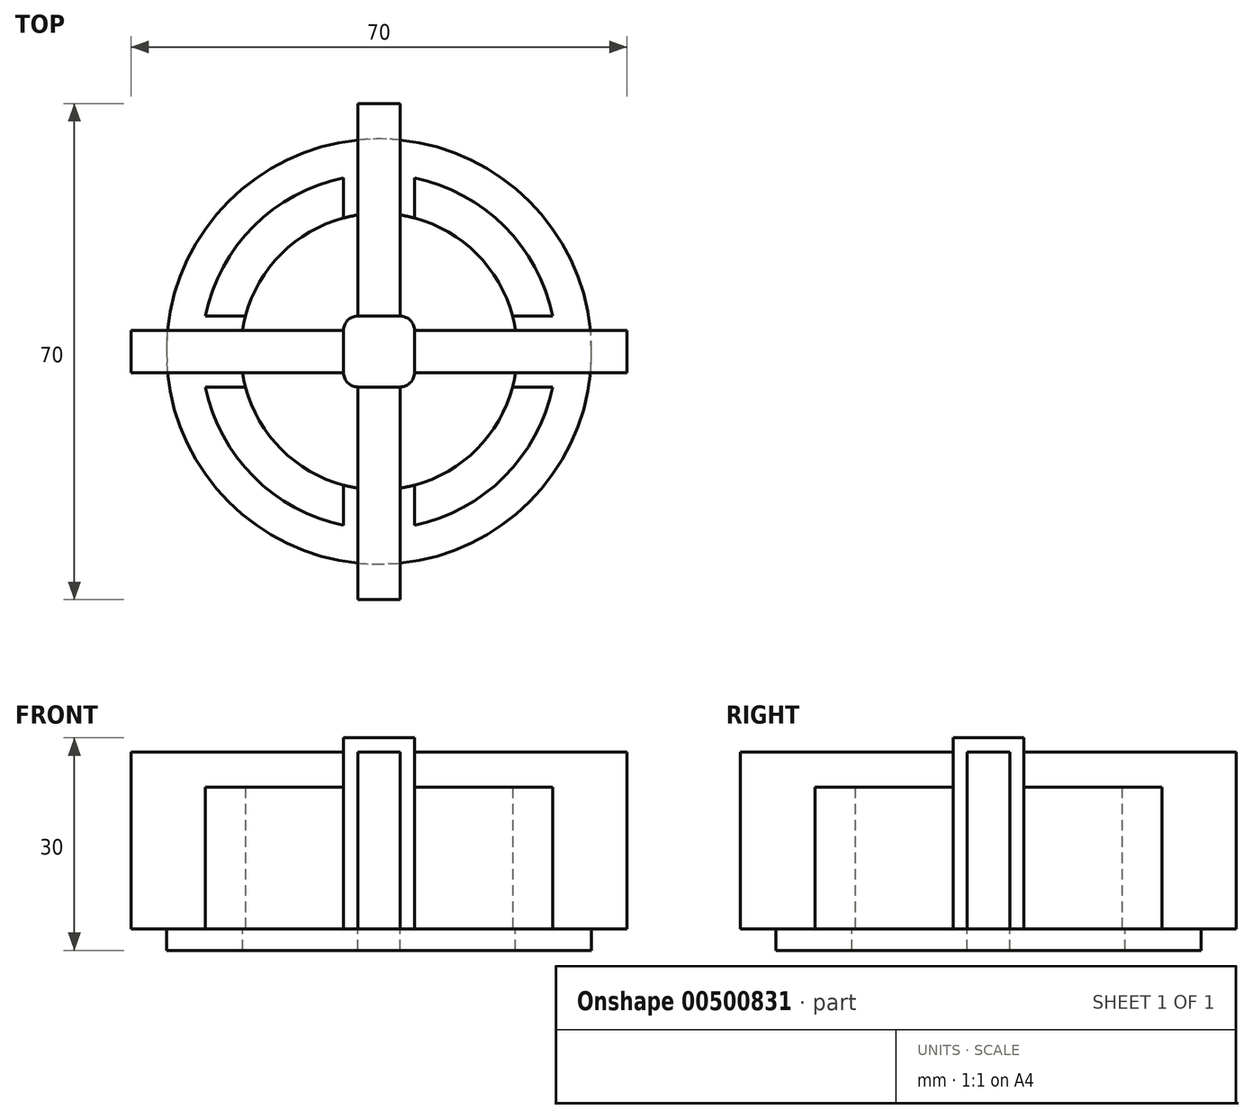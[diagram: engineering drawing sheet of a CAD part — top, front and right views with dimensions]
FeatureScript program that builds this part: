
annotation { "Feature Type Name" : "Feature", "Feature Type Description" : "" }
export const myFeature = defineFeature(function(context is Context, id is Id, definition is map)
    precondition{}
    {
        {
            var Q0;
            Q0=qCreatedBy(makeId("Top.planeOp"),FACE);
            var sketch = newSketch(context, id + "F0", { "sketchPlane" : qUnion([Q0])});
            skCircle(sketch, "E0", {"center": v(0, 0) * mm, "radius": 25 * mm});
            skCircle(sketch, "E1.0", {"center": v(0, 0) * mm, "radius": 19.5 * mm});
            skLineSegment(sketch, "E2", {"start": v(0, 0) * mm, "end": v(0, -5) * mm, "construction": true});
            skLineSegment(sketch, "E3", {"start": v(-3, -5) * mm, "end": v(3, -5) * mm});
            skPoint(sketch, "E4", {"position": v(0, -5) * mm});
            skLineSegment(sketch, "E5", {"start": v(5, -3) * mm, "end": v(5, 3) * mm});
            skLineSegment(sketch, "E6", {"start": v(3, 5) * mm, "end": v(-3, 5) * mm});
            skLineSegment(sketch, "E7", {"start": v(-5, 3) * mm, "end": v(-5, -3) * mm});
            skLineSegment(sketch, "E8", {"start": v(-3, -5) * mm, "end": v(3, -5) * mm, "construction": true});
            skLineSegment(sketch, "E9", {"start": v(-3, -5) * mm, "end": v(-3, -35) * mm});
            skLineSegment(sketch, "E10", {"start": v(-3, -35) * mm, "end": v(3, -35) * mm});
            skLineSegment(sketch, "E11", {"start": v(3, -35) * mm, "end": v(3, -5) * mm});
            skLineSegment(sketch, "E12", {"start": v(5, 3) * mm, "end": v(5, -3) * mm, "construction": true});
            skPoint(sketch, "E13", {"position": v(5, 0) * mm});
            skLineSegment(sketch, "E14", {"start": v(0, 0) * mm, "end": v(5, 0) * mm, "construction": true});
            skLineSegment(sketch, "E15", {"start": v(5, 3) * mm, "end": v(35, 3) * mm});
            skLineSegment(sketch, "E16", {"start": v(35, 3) * mm, "end": v(35, -3) * mm});
            skLineSegment(sketch, "E17", {"start": v(35, -3) * mm, "end": v(5, -3) * mm});
            skLineSegment(sketch, "E18", {"start": v(0, -35) * mm, "end": v(0, -30) * mm, "construction": true});
            skLineSegment(sketch, "E19", {"start": v(3, -30) * mm, "end": v(-3, -30) * mm, "construction": true});
            skLineSegment(sketch, "E20", {"start": v(35, 0) * mm, "end": v(30, 0) * mm, "construction": true});
            skLineSegment(sketch, "E21", {"start": v(30, -3) * mm, "end": v(30, 3) * mm, "construction": true});
            skLineSegment(sketch, "E22", {"start": v(24.5, 0) * mm, "end": v(24.5, 5) * mm, "construction": true});
            skLineSegment(sketch, "E23", {"start": v(24.5, 5) * mm, "end": v(18.85, 5) * mm});
            skLineSegment(sketch, "E24.MirrorCS", {"start": v(24.5, 0) * mm, "end": v(24.5, -5) * mm, "construction": true});
            skLineSegment(sketch, "E25.MirrorCS", {"start": v(24.5, -5) * mm, "end": v(18.85, -5) * mm});
            skLineSegment(sketch, "E26", {"start": v(0, -24.5) * mm, "end": v(5, -24.5) * mm, "construction": true});
            skPoint(sketch, "E27.visualSharp", {"position": v(5, -5) * mm});
            skArc(sketch, "E27.filletArc", {"start": v(3, -5) * mm, "mid": v(4.41, -4.41) * mm, "end": v(5, -3) * mm});
            skPoint(sketch, "E28.visualSharp", {"position": v(5, 5) * mm});
            skArc(sketch, "E28.filletArc", {"start": v(5, 3) * mm, "mid": v(4.41, 4.41) * mm, "end": v(3, 5) * mm});
            skPoint(sketch, "E29.visualSharp", {"position": v(-5, 5) * mm});
            skArc(sketch, "E29.filletArc", {"start": v(-3, 5) * mm, "mid": v(-4.41, 4.41) * mm, "end": v(-5, 3) * mm});
            skPoint(sketch, "E30.visualSharp", {"position": v(-5, -5) * mm});
            skArc(sketch, "E30.filletArc", {"start": v(-5, -3) * mm, "mid": v(-4.41, -4.41) * mm, "end": v(-3, -5) * mm});
            skLineSegment(sketch, "E31.MirrorCS", {"start": v(3, 35) * mm, "end": v(3, 5) * mm});
            skLineSegment(sketch, "E32.MirrorCS", {"start": v(-3, 5) * mm, "end": v(-3, 35) * mm});
            skLineSegment(sketch, "E33.MirrorCS", {"start": v(3, 30) * mm, "end": v(-3, 30) * mm, "construction": true});
            skLineSegment(sketch, "E34.MirrorCS", {"start": v(0, 35) * mm, "end": v(0, 30) * mm, "construction": true});
            skLineSegment(sketch, "E35.MirrorCS", {"start": v(-3, 35) * mm, "end": v(3, 35) * mm});
            skLineSegment(sketch, "E36.MirrorCS", {"start": v(0, -24.5) * mm, "end": v(-5, -24.5) * mm, "construction": true});
            skLineSegment(sketch, "E37", {"start": v(5, -24.5) * mm, "end": v(5, -18.85) * mm});
            skLineSegment(sketch, "E38.MirrorCS", {"start": v(-5, -24.5) * mm, "end": v(-5, -18.85) * mm});
            skLineSegment(sketch, "E39.MirrorCS", {"start": v(5, 24.5) * mm, "end": v(5, 18.85) * mm});
            skLineSegment(sketch, "E40.MirrorCS", {"start": v(-5, 24.5) * mm, "end": v(-5, 18.85) * mm});
            skLineSegment(sketch, "E41.MirrorCS", {"start": v(-35, -3) * mm, "end": v(-5, -3) * mm});
            skLineSegment(sketch, "E42.MirrorCS", {"start": v(-5, 3) * mm, "end": v(-35, 3) * mm});
            skLineSegment(sketch, "E43.MirrorCS", {"start": v(-24.5, -5) * mm, "end": v(-18.85, -5) * mm});
            skLineSegment(sketch, "E44.MirrorCS", {"start": v(-24.5, 5) * mm, "end": v(-18.85, 5) * mm});
            skLineSegment(sketch, "E45.MirrorCS", {"start": v(-30, -3) * mm, "end": v(-30, 3) * mm, "construction": true});
            skLineSegment(sketch, "E46.MirrorCS", {"start": v(-35, 3) * mm, "end": v(-35, -3) * mm});
            skCircle(sketch, "E47", {"center": v(0, 0) * mm, "radius": 30 * mm});
            skSolve(sketch);
        }
        {
            var Q0;
            {var subQ0=sQuery(id+"F0.wireOp",EDGE,"E0");var subQ4=makeQuery(id+"F0.imprint","INTERSECT",VERTEX,{"derivedFrom":[subQ0,sQuery(id+"F0.wireOp",EDGE,"E37")]});Q0=makeQuery(id+"F0.imprint","IMPRINT",FACE,{"disambiguationData":[TD([[makeQuery(id+"F0.imprint","IMPRINT",EDGE,{"disambiguationData":[TD([[subQ4,1.0]])],"derivedFrom":subQ0}),-1.0]])]});}
            var Q1;
            {var subQ0=sQuery(id+"F0.wireOp",EDGE,"E25.MirrorCS");Q1=makeQuery(id+"F0.imprint","IMPRINT",FACE,{"disambiguationData":[TD([[makeQuery(id+"F0.imprint","IMPRINT",EDGE,{"derivedFrom":subQ0}),1.0]])]});}
            var Q2;
            {var subQ0=sQuery(id+"F0.wireOp",EDGE,"E25.MirrorCS");Q2=makeQuery(id+"F0.imprint","IMPRINT",FACE,{"disambiguationData":[TD([[makeQuery(id+"F0.imprint","IMPRINT",EDGE,{"derivedFrom":subQ0}),-1.0]])]});}
            var Q3;
            {var subQ0=sQuery(id+"F0.wireOp",EDGE,"E15");var subQ1=sQuery(id+"F0.wireOp",EDGE,"E0");var subQ2=makeQuery(id+"F0.imprint","INTERSECT",VERTEX,{"derivedFrom":[subQ1,subQ0]});Q3=makeQuery(id+"F0.imprint","IMPRINT",FACE,{"disambiguationData":[TD([[makeQuery(id+"F0.imprint","IMPRINT",EDGE,{"disambiguationData":[TD([[subQ2,1.0]])],"derivedFrom":subQ1}),1.0]])]});}
            var Q4;
            {var subQ0=sQuery(id+"F0.wireOp",EDGE,"E23");Q4=makeQuery(id+"F0.imprint","IMPRINT",FACE,{"disambiguationData":[TD([[makeQuery(id+"F0.imprint","IMPRINT",EDGE,{"derivedFrom":subQ0}),1.0]])]});}
            var Q5;
            {var subQ0=sQuery(id+"F0.wireOp",EDGE,"E23");Q5=makeQuery(id+"F0.imprint","IMPRINT",FACE,{"disambiguationData":[TD([[makeQuery(id+"F0.imprint","IMPRINT",EDGE,{"derivedFrom":subQ0}),-1.0]])]});}
            var Q6;
            {var subQ3=sQuery(id+"F0.wireOp",EDGE,"E0");var subQ8=makeQuery(id+"F0.imprint","INTERSECT",VERTEX,{"derivedFrom":[subQ3,sQuery(id+"F0.wireOp",EDGE,"E23")]});Q6=makeQuery(id+"F0.imprint","IMPRINT",FACE,{"disambiguationData":[TD([[makeQuery(id+"F0.imprint","IMPRINT",EDGE,{"disambiguationData":[TD([[subQ8,1.0]])],"derivedFrom":subQ3}),-1.0]])]});}
            var Q7;
            {var subQ0=sQuery(id+"F0.wireOp",EDGE,"E15");var subQ1=sQuery(id+"F0.wireOp",EDGE,"E0");var subQ2=makeQuery(id+"F0.imprint","INTERSECT",VERTEX,{"derivedFrom":[subQ1,subQ0]});Q7=makeQuery(id+"F0.imprint","IMPRINT",FACE,{"disambiguationData":[TD([[makeQuery(id+"F0.imprint","IMPRINT",EDGE,{"disambiguationData":[TD([[subQ2,1.0]])],"derivedFrom":subQ1}),-1.0]])]});}
            var Q8;
            {var subQ0=sQuery(id+"F0.wireOp",EDGE,"E9");var subQ1=sQuery(id+"F0.wireOp",EDGE,"E0");var subQ2=makeQuery(id+"F0.imprint","INTERSECT",VERTEX,{"derivedFrom":[subQ1,subQ0]});Q8=makeQuery(id+"F0.imprint","IMPRINT",FACE,{"disambiguationData":[TD([[makeQuery(id+"F0.imprint","IMPRINT",EDGE,{"disambiguationData":[TD([[subQ2,-1.0]])],"derivedFrom":subQ1}),-1.0]])]});}
            var Q9;
            {var subQ0=sQuery(id+"F0.wireOp",EDGE,"E9");var subQ1=sQuery(id+"F0.wireOp",EDGE,"E0");var subQ2=makeQuery(id+"F0.imprint","INTERSECT",VERTEX,{"derivedFrom":[subQ1,subQ0]});Q9=makeQuery(id+"F0.imprint","IMPRINT",FACE,{"disambiguationData":[TD([[makeQuery(id+"F0.imprint","IMPRINT",EDGE,{"disambiguationData":[TD([[subQ2,-1.0]])],"derivedFrom":subQ1}),1.0]])]});}
            var Q10;
            {var subQ0=sQuery(id+"F0.wireOp",EDGE,"E37");Q10=makeQuery(id+"F0.imprint","IMPRINT",FACE,{"disambiguationData":[TD([[makeQuery(id+"F0.imprint","IMPRINT",EDGE,{"derivedFrom":subQ0}),1.0]])]});}
            var Q11;
            {var subQ0=sQuery(id+"F0.wireOp",EDGE,"E38.MirrorCS");Q11=makeQuery(id+"F0.imprint","IMPRINT",FACE,{"disambiguationData":[TD([[makeQuery(id+"F0.imprint","IMPRINT",EDGE,{"derivedFrom":subQ0}),-1.0]])]});}
            var Q12;
            {var subQ0=sQuery(id+"F0.wireOp",EDGE,"E0");var subQ4=makeQuery(id+"F0.imprint","INTERSECT",VERTEX,{"derivedFrom":[subQ0,sQuery(id+"F0.wireOp",EDGE,"E43.MirrorCS")]});Q12=makeQuery(id+"F0.imprint","IMPRINT",FACE,{"disambiguationData":[TD([[makeQuery(id+"F0.imprint","IMPRINT",EDGE,{"disambiguationData":[TD([[subQ4,1.0]])],"derivedFrom":subQ0}),-1.0]])]});}
            var Q13;
            {var subQ0=sQuery(id+"F0.wireOp",EDGE,"E38.MirrorCS");Q13=makeQuery(id+"F0.imprint","IMPRINT",FACE,{"disambiguationData":[TD([[makeQuery(id+"F0.imprint","IMPRINT",EDGE,{"derivedFrom":subQ0}),1.0]])]});}
            var Q14;
            {var subQ0=sQuery(id+"F0.wireOp",EDGE,"E43.MirrorCS");Q14=makeQuery(id+"F0.imprint","IMPRINT",FACE,{"disambiguationData":[TD([[makeQuery(id+"F0.imprint","IMPRINT",EDGE,{"derivedFrom":subQ0}),1.0]])]});}
            var Q15;
            {var subQ0=sQuery(id+"F0.wireOp",EDGE,"E42.MirrorCS");var subQ1=sQuery(id+"F0.wireOp",EDGE,"E0");var subQ2=makeQuery(id+"F0.imprint","INTERSECT",VERTEX,{"derivedFrom":[subQ1,subQ0]});Q15=makeQuery(id+"F0.imprint","IMPRINT",FACE,{"disambiguationData":[TD([[makeQuery(id+"F0.imprint","IMPRINT",EDGE,{"disambiguationData":[TD([[subQ2,-1.0]])],"derivedFrom":subQ1}),1.0]])]});}
            var Q16;
            {var subQ0=sQuery(id+"F0.wireOp",EDGE,"E44.MirrorCS");Q16=makeQuery(id+"F0.imprint","IMPRINT",FACE,{"disambiguationData":[TD([[makeQuery(id+"F0.imprint","IMPRINT",EDGE,{"derivedFrom":subQ0}),-1.0]])]});}
            var Q17;
            {var subQ3=sQuery(id+"F0.wireOp",EDGE,"E0");var subQ8=makeQuery(id+"F0.imprint","INTERSECT",VERTEX,{"derivedFrom":[subQ3,sQuery(id+"F0.wireOp",EDGE,"E40.MirrorCS")]});Q17=makeQuery(id+"F0.imprint","IMPRINT",FACE,{"disambiguationData":[TD([[makeQuery(id+"F0.imprint","IMPRINT",EDGE,{"disambiguationData":[TD([[subQ8,1.0]])],"derivedFrom":subQ3}),-1.0]])]});}
            var Q18;
            {var subQ0=sQuery(id+"F0.wireOp",EDGE,"E40.MirrorCS");Q18=makeQuery(id+"F0.imprint","IMPRINT",FACE,{"disambiguationData":[TD([[makeQuery(id+"F0.imprint","IMPRINT",EDGE,{"derivedFrom":subQ0}),-1.0]])]});}
            var Q19;
            {var subQ0=sQuery(id+"F0.wireOp",EDGE,"E40.MirrorCS");Q19=makeQuery(id+"F0.imprint","IMPRINT",FACE,{"disambiguationData":[TD([[makeQuery(id+"F0.imprint","IMPRINT",EDGE,{"derivedFrom":subQ0}),1.0]])]});}
            var Q20;
            {var subQ0=sQuery(id+"F0.wireOp",EDGE,"E31.MirrorCS");var subQ1=sQuery(id+"F0.wireOp",EDGE,"E0");var subQ2=makeQuery(id+"F0.imprint","INTERSECT",VERTEX,{"derivedFrom":[subQ1,subQ0]});Q20=makeQuery(id+"F0.imprint","IMPRINT",FACE,{"disambiguationData":[TD([[makeQuery(id+"F0.imprint","IMPRINT",EDGE,{"disambiguationData":[TD([[subQ2,-1.0]])],"derivedFrom":subQ1}),1.0]])]});}
            var Q21;
            {var subQ0=sQuery(id+"F0.wireOp",EDGE,"E39.MirrorCS");Q21=makeQuery(id+"F0.imprint","IMPRINT",FACE,{"disambiguationData":[TD([[makeQuery(id+"F0.imprint","IMPRINT",EDGE,{"derivedFrom":subQ0}),-1.0]])]});}
            var Q22;
            {var subQ0=sQuery(id+"F0.wireOp",EDGE,"E31.MirrorCS");var subQ1=sQuery(id+"F0.wireOp",EDGE,"E0");var subQ2=makeQuery(id+"F0.imprint","INTERSECT",VERTEX,{"derivedFrom":[subQ1,subQ0]});Q22=makeQuery(id+"F0.imprint","IMPRINT",FACE,{"disambiguationData":[TD([[makeQuery(id+"F0.imprint","IMPRINT",EDGE,{"disambiguationData":[TD([[subQ2,-1.0]])],"derivedFrom":subQ1}),-1.0]])]});}
            var Q23;
            {var subQ0=sQuery(id+"F0.wireOp",EDGE,"E42.MirrorCS");var subQ1=sQuery(id+"F0.wireOp",EDGE,"E0");var subQ2=makeQuery(id+"F0.imprint","INTERSECT",VERTEX,{"derivedFrom":[subQ1,subQ0]});Q23=makeQuery(id+"F0.imprint","IMPRINT",FACE,{"disambiguationData":[TD([[makeQuery(id+"F0.imprint","IMPRINT",EDGE,{"disambiguationData":[TD([[subQ2,-1.0]])],"derivedFrom":subQ1}),-1.0]])]});}
            var Q24;
            {var subQ5=sQuery(id+"F0.wireOp",EDGE,"E3");Q24=makeQuery(id+"F0.imprint","IMPRINT",FACE,{"disambiguationData":[TD([[makeQuery(id+"F0.imprint","IMPRINT",EDGE,{"derivedFrom":subQ5}),-1.0]])]});}
            var Q25;
            {var subQ5=sQuery(id+"F0.wireOp",EDGE,"E5");Q25=makeQuery(id+"F0.imprint","IMPRINT",FACE,{"disambiguationData":[TD([[makeQuery(id+"F0.imprint","IMPRINT",EDGE,{"derivedFrom":subQ5}),-1.0]])]});}
            var Q26;
            {var subQ5=sQuery(id+"F0.wireOp",EDGE,"E6");Q26=makeQuery(id+"F0.imprint","IMPRINT",FACE,{"disambiguationData":[TD([[makeQuery(id+"F0.imprint","IMPRINT",EDGE,{"derivedFrom":subQ5}),-1.0]])]});}
            var Q27;
            {var subQ5=sQuery(id+"F0.wireOp",EDGE,"E7");Q27=makeQuery(id+"F0.imprint","IMPRINT",FACE,{"disambiguationData":[TD([[makeQuery(id+"F0.imprint","IMPRINT",EDGE,{"derivedFrom":subQ5}),-1.0]])]});}
            var Q28;
            Q28=makeQuery(id+"F0.imprint","IMPRINT",FACE,{"disambiguationData":[TD([[makeQuery(id+"F0.imprint","IMPRINT",EDGE,{"derivedFrom":sQuery(id+"F0.wireOp",EDGE,"E3")}),1.0]])]});
            extrude(context, id + "F1", {"entities" : qUnion([Q0, Q1, Q2, Q3, Q4, Q5, Q6, Q7, Q8, Q9, Q10, Q11, Q12, Q13, Q14, Q15, Q16, Q17, Q18, Q19, Q20, Q21, Q22, Q23, Q24, Q25, Q26, Q27, Q28]), "oppositeDirection" : true, "depth" : 3 * mm});
        }
        {
            var Q0;
            {var subQ0=sQuery(id+"F0.wireOp",EDGE,"E40.MirrorCS");Q0=makeQuery(id+"F0.imprint","IMPRINT",FACE,{"disambiguationData":[TD([[makeQuery(id+"F0.imprint","IMPRINT",EDGE,{"derivedFrom":subQ0}),-1.0]])]});}
            var Q1;
            {var subQ0=sQuery(id+"F0.wireOp",EDGE,"E23");Q1=makeQuery(id+"F0.imprint","IMPRINT",FACE,{"disambiguationData":[TD([[makeQuery(id+"F0.imprint","IMPRINT",EDGE,{"derivedFrom":subQ0}),-1.0]])]});}
            var Q2;
            {var subQ0=sQuery(id+"F0.wireOp",EDGE,"E25.MirrorCS");Q2=makeQuery(id+"F0.imprint","IMPRINT",FACE,{"disambiguationData":[TD([[makeQuery(id+"F0.imprint","IMPRINT",EDGE,{"derivedFrom":subQ0}),1.0]])]});}
            var Q3;
            {var subQ0=sQuery(id+"F0.wireOp",EDGE,"E38.MirrorCS");Q3=makeQuery(id+"F0.imprint","IMPRINT",FACE,{"disambiguationData":[TD([[makeQuery(id+"F0.imprint","IMPRINT",EDGE,{"derivedFrom":subQ0}),1.0]])]});}
            extrude(context, id + "F2", {"entities" : qUnion([Q0, Q1, Q2, Q3]), "operationType" : NewBodyOperationType.ADD, "depth" : 20 * mm});
        }
        {
            var Q0;
            {var subQ5=sQuery(id+"F0.wireOp",EDGE,"E7");Q0=makeQuery(id+"F0.imprint","IMPRINT",FACE,{"disambiguationData":[TD([[makeQuery(id+"F0.imprint","IMPRINT",EDGE,{"derivedFrom":subQ5}),-1.0]])]});}
            var Q1;
            {var subQ0=sQuery(id+"F0.wireOp",EDGE,"E42.MirrorCS");var subQ1=sQuery(id+"F0.wireOp",EDGE,"E0");var subQ2=makeQuery(id+"F0.imprint","INTERSECT",VERTEX,{"derivedFrom":[subQ1,subQ0]});Q1=makeQuery(id+"F0.imprint","IMPRINT",FACE,{"disambiguationData":[TD([[makeQuery(id+"F0.imprint","IMPRINT",EDGE,{"disambiguationData":[TD([[subQ2,-1.0]])],"derivedFrom":subQ1}),1.0]])]});}
            var Q2;
            {var subQ0=sQuery(id+"F0.wireOp",EDGE,"E42.MirrorCS");var subQ1=sQuery(id+"F0.wireOp",EDGE,"E0");var subQ2=makeQuery(id+"F0.imprint","INTERSECT",VERTEX,{"derivedFrom":[subQ1,subQ0]});Q2=makeQuery(id+"F0.imprint","IMPRINT",FACE,{"disambiguationData":[TD([[makeQuery(id+"F0.imprint","IMPRINT",EDGE,{"disambiguationData":[TD([[subQ2,-1.0]])],"derivedFrom":subQ1}),-1.0]])]});}
            var Q3;
            {var subQ0=sQuery(id+"F0.wireOp",EDGE,"E46.MirrorCS");Q3=makeQuery(id+"F0.imprint","IMPRINT",FACE,{"disambiguationData":[TD([[makeQuery(id+"F0.imprint","IMPRINT",EDGE,{"derivedFrom":subQ0}),1.0]])]});}
            var Q4;
            {var subQ0=sQuery(id+"F0.wireOp",EDGE,"E10");Q4=makeQuery(id+"F0.imprint","IMPRINT",FACE,{"disambiguationData":[TD([[makeQuery(id+"F0.imprint","IMPRINT",EDGE,{"derivedFrom":subQ0}),1.0]])]});}
            var Q5;
            {var subQ0=sQuery(id+"F0.wireOp",EDGE,"E9");var subQ1=sQuery(id+"F0.wireOp",EDGE,"E0");var subQ2=makeQuery(id+"F0.imprint","INTERSECT",VERTEX,{"derivedFrom":[subQ1,subQ0]});Q5=makeQuery(id+"F0.imprint","IMPRINT",FACE,{"disambiguationData":[TD([[makeQuery(id+"F0.imprint","IMPRINT",EDGE,{"disambiguationData":[TD([[subQ2,-1.0]])],"derivedFrom":subQ1}),-1.0]])]});}
            var Q6;
            {var subQ0=sQuery(id+"F0.wireOp",EDGE,"E9");var subQ1=sQuery(id+"F0.wireOp",EDGE,"E0");var subQ2=makeQuery(id+"F0.imprint","INTERSECT",VERTEX,{"derivedFrom":[subQ1,subQ0]});Q6=makeQuery(id+"F0.imprint","IMPRINT",FACE,{"disambiguationData":[TD([[makeQuery(id+"F0.imprint","IMPRINT",EDGE,{"disambiguationData":[TD([[subQ2,-1.0]])],"derivedFrom":subQ1}),1.0]])]});}
            var Q7;
            {var subQ5=sQuery(id+"F0.wireOp",EDGE,"E3");Q7=makeQuery(id+"F0.imprint","IMPRINT",FACE,{"disambiguationData":[TD([[makeQuery(id+"F0.imprint","IMPRINT",EDGE,{"derivedFrom":subQ5}),-1.0]])]});}
            var Q8;
            {var subQ5=sQuery(id+"F0.wireOp",EDGE,"E5");Q8=makeQuery(id+"F0.imprint","IMPRINT",FACE,{"disambiguationData":[TD([[makeQuery(id+"F0.imprint","IMPRINT",EDGE,{"derivedFrom":subQ5}),-1.0]])]});}
            var Q9;
            {var subQ0=sQuery(id+"F0.wireOp",EDGE,"E15");var subQ1=sQuery(id+"F0.wireOp",EDGE,"E0");var subQ2=makeQuery(id+"F0.imprint","INTERSECT",VERTEX,{"derivedFrom":[subQ1,subQ0]});Q9=makeQuery(id+"F0.imprint","IMPRINT",FACE,{"disambiguationData":[TD([[makeQuery(id+"F0.imprint","IMPRINT",EDGE,{"disambiguationData":[TD([[subQ2,1.0]])],"derivedFrom":subQ1}),1.0]])]});}
            var Q10;
            {var subQ0=sQuery(id+"F0.wireOp",EDGE,"E15");var subQ1=sQuery(id+"F0.wireOp",EDGE,"E0");var subQ2=makeQuery(id+"F0.imprint","INTERSECT",VERTEX,{"derivedFrom":[subQ1,subQ0]});Q10=makeQuery(id+"F0.imprint","IMPRINT",FACE,{"disambiguationData":[TD([[makeQuery(id+"F0.imprint","IMPRINT",EDGE,{"disambiguationData":[TD([[subQ2,1.0]])],"derivedFrom":subQ1}),-1.0]])]});}
            var Q11;
            {var subQ0=sQuery(id+"F0.wireOp",EDGE,"E16");Q11=makeQuery(id+"F0.imprint","IMPRINT",FACE,{"disambiguationData":[TD([[makeQuery(id+"F0.imprint","IMPRINT",EDGE,{"derivedFrom":subQ0}),-1.0]])]});}
            var Q12;
            {var subQ5=sQuery(id+"F0.wireOp",EDGE,"E6");Q12=makeQuery(id+"F0.imprint","IMPRINT",FACE,{"disambiguationData":[TD([[makeQuery(id+"F0.imprint","IMPRINT",EDGE,{"derivedFrom":subQ5}),-1.0]])]});}
            var Q13;
            {var subQ0=sQuery(id+"F0.wireOp",EDGE,"E31.MirrorCS");var subQ1=sQuery(id+"F0.wireOp",EDGE,"E0");var subQ2=makeQuery(id+"F0.imprint","INTERSECT",VERTEX,{"derivedFrom":[subQ1,subQ0]});Q13=makeQuery(id+"F0.imprint","IMPRINT",FACE,{"disambiguationData":[TD([[makeQuery(id+"F0.imprint","IMPRINT",EDGE,{"disambiguationData":[TD([[subQ2,-1.0]])],"derivedFrom":subQ1}),1.0]])]});}
            var Q14;
            {var subQ0=sQuery(id+"F0.wireOp",EDGE,"E31.MirrorCS");var subQ1=sQuery(id+"F0.wireOp",EDGE,"E0");var subQ2=makeQuery(id+"F0.imprint","INTERSECT",VERTEX,{"derivedFrom":[subQ1,subQ0]});Q14=makeQuery(id+"F0.imprint","IMPRINT",FACE,{"disambiguationData":[TD([[makeQuery(id+"F0.imprint","IMPRINT",EDGE,{"disambiguationData":[TD([[subQ2,-1.0]])],"derivedFrom":subQ1}),-1.0]])]});}
            var Q15;
            {var subQ0=sQuery(id+"F0.wireOp",EDGE,"E35.MirrorCS");Q15=makeQuery(id+"F0.imprint","IMPRINT",FACE,{"disambiguationData":[TD([[makeQuery(id+"F0.imprint","IMPRINT",EDGE,{"derivedFrom":subQ0}),-1.0]])]});}
            extrude(context, id + "F3", {"entities" : qUnion([Q0, Q1, Q2, Q3, Q4, Q5, Q6, Q7, Q8, Q9, Q10, Q11, Q12, Q13, Q14, Q15]), "operationType" : NewBodyOperationType.ADD, "depth" : 25 * mm});
        }
        {
            var Q0;
            Q0=makeQuery(id+"F0.imprint","IMPRINT",FACE,{"disambiguationData":[TD([[makeQuery(id+"F0.imprint","IMPRINT",EDGE,{"derivedFrom":sQuery(id+"F0.wireOp",EDGE,"E3")}),1.0]])]});
            extrude(context, id + "F4", {"entities" : qUnion([Q0]), "operationType" : NewBodyOperationType.ADD, "depth" : 27 * mm});
        }
    });
